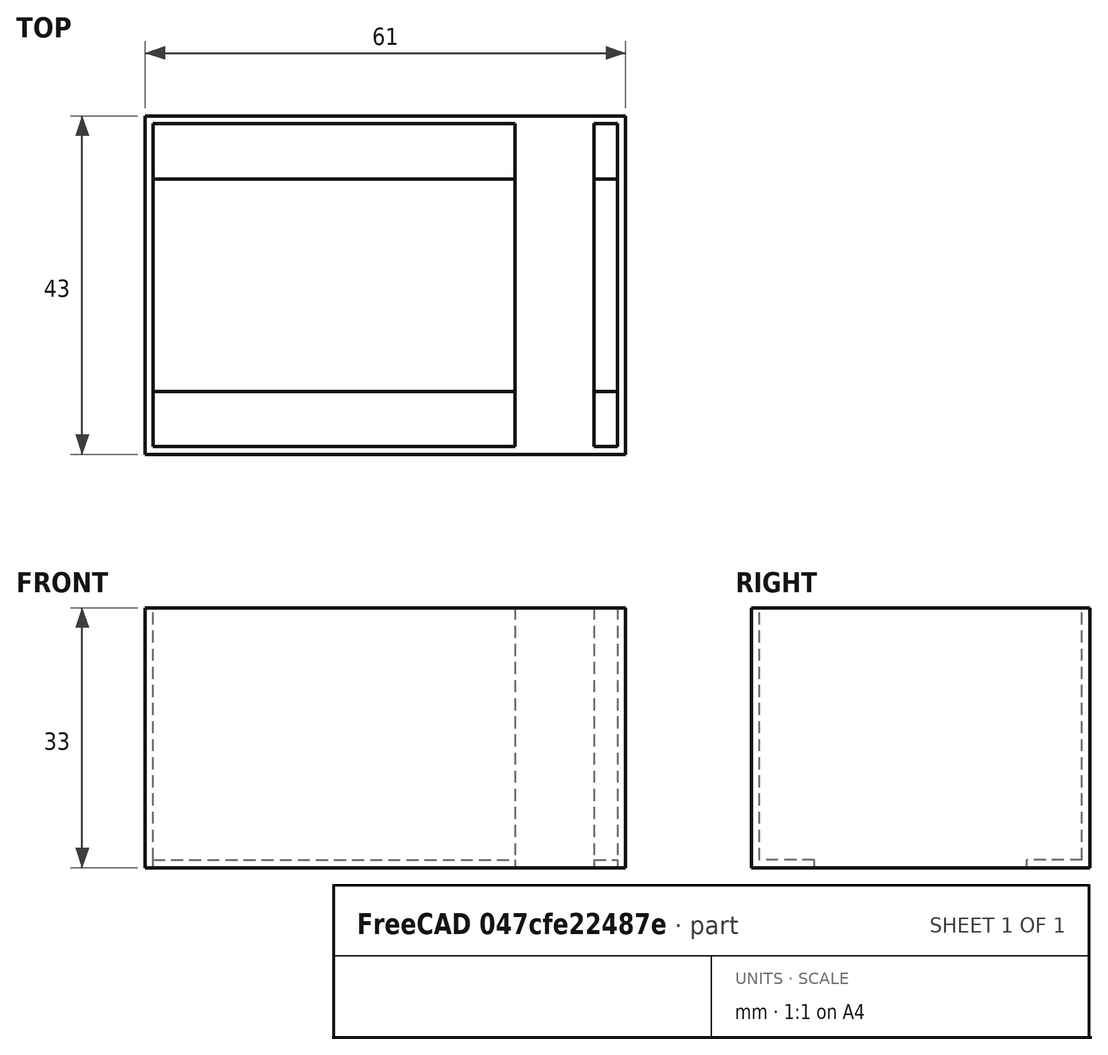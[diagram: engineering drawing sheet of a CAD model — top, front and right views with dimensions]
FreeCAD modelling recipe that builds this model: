
FCSTD DOCUMENT  (FreeCAD 0.18R4 (GitTag))
Label: highlands
License: All rights reserved
LicenseURL: http://en.wikipedia.org/wiki/All_rights_reserved
objects: Part::Box×7, Part::Cut×2, Part::MultiFuse×2
note: 11 computed .brp shape members not serialized (recipe doc carries the construction recipe); baked Part::Feature solids carry a one-line shape summary decoded from their .brp

FEATURE [Part::Box] Box  label="Cube"
  AttacherType = Attacher::AttachEngine3D
  Height = 33
  Length = 202
  Width = 43
FEATURE [Part::Box] Box001  label="Cube001"
  AttacherType = Attacher::AttachEngine3D
  Height = 33
  Length = 200
  Placement = pos=(1,1,0) rot=(0,0,1;0rad)
  Width = 41
FEATURE [Part::Cut] Cut
  Base = -> Box
  Tool = -> Box001
FEATURE [Part::Box] Box002  label="Cube002"
  AttacherType = Attacher::AttachEngine3D
  Height = 1
  Length = 202
  Width = 8
FEATURE [Part::Box] Box003  label="Cube003"
  AttacherType = Attacher::AttachEngine3D
  Height = 1
  Length = 202
  Placement = pos=(0,35,0) rot=(0,0,1;0rad)
  Width = 8
FEATURE [Part::MultiFuse] Fusion
  Shapes = -> [Cut,Box002,Box003]
FEATURE [Part::Box] Box004  label="Cube004"
  AttacherType = Attacher::AttachEngine3D
  Height = 33
  Length = 10
  Placement = pos=(47,0,0) rot=(0,0,1;0rad)
  Width = 43
FEATURE [Part::Box] Box005  label="Cube005"
  AttacherType = Attacher::AttachEngine3D
  Height = 33
  Length = 10
  Placement = pos=(60,0,0) rot=(0,0,1;0rad)
  Width = 43
FEATURE [Part::Box] Box006  label="Cube006"
  AttacherType = Attacher::AttachEngine3D
  Height = 33
  Length = 141
  Placement = pos=(61,0,0) rot=(0,0,1;0rad)
  Width = 43
FEATURE [Part::MultiFuse] Fusion001
  Shapes = -> [Fusion,Box004,Box005]
FEATURE [Part::Cut] Cut001
  Base = -> Fusion001
  Tool = -> Box006
